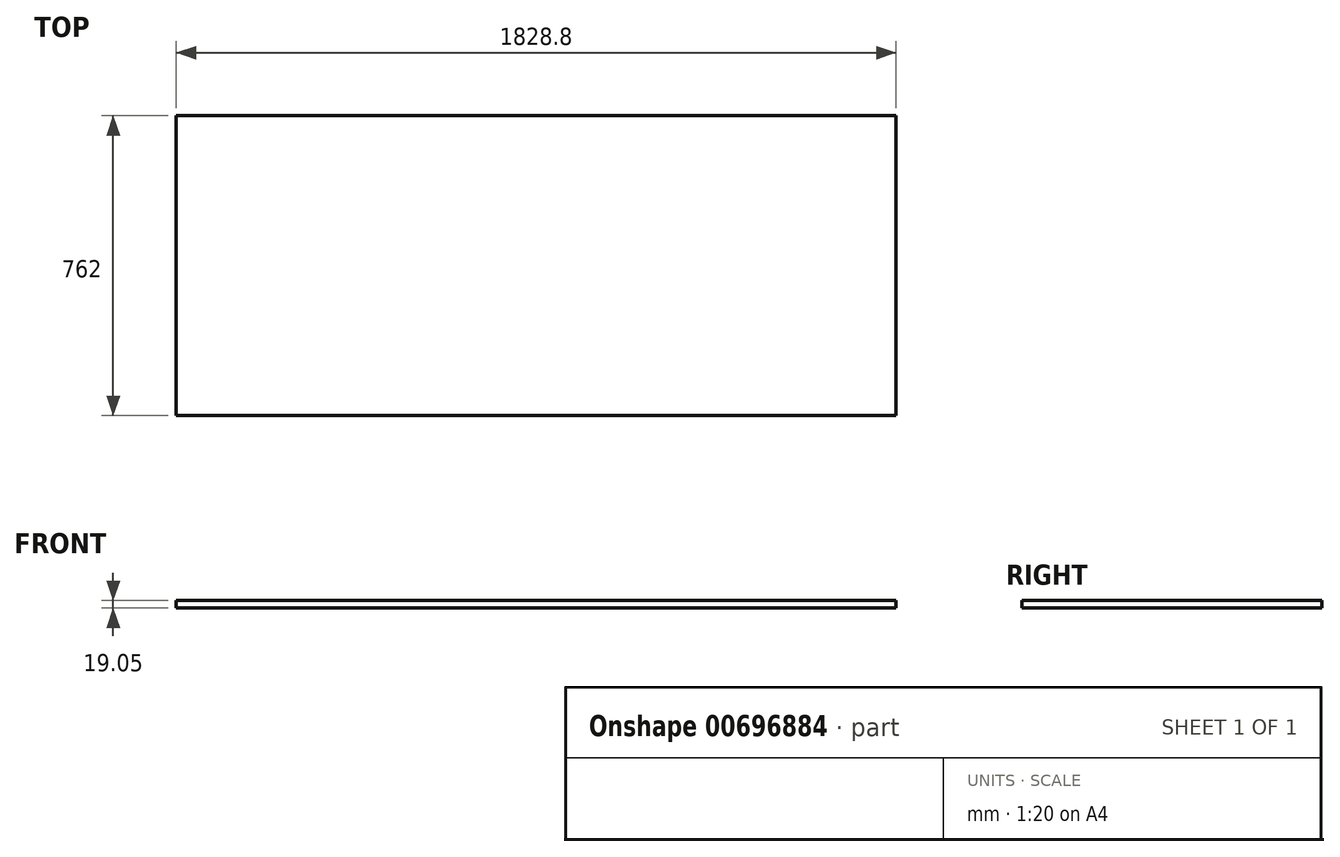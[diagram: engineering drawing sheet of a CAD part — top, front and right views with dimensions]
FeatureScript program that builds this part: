
annotation { "Feature Type Name" : "Feature", "Feature Type Description" : "" }
export const myFeature = defineFeature(function(context is Context, id is Id, definition is map)
    precondition{}
    {
        {
            var Q0;
            Q0=qCreatedBy(makeId("Top.planeOp"),FACE);
            var sketch = newSketch(context, id + "F0", { "sketchPlane" : qUnion([Q0])});
            skLineSegment(sketch, "E0.bottom", {"start": v(914.4, -381) * mm, "end": v(-914.4, -381) * mm});
            skLineSegment(sketch, "E0.top", {"start": v(914.4, 381) * mm, "end": v(-914.4, 381) * mm});
            skLineSegment(sketch, "E0.left", {"start": v(914.4, -381) * mm, "end": v(914.4, 381) * mm});
            skLineSegment(sketch, "E0.right", {"start": v(-914.4, -381) * mm, "end": v(-914.4, 381) * mm});
            skPoint(sketch, "E0.middle", {"position": v(0, 0) * mm});
            skSolve(sketch);
        }
        {
            var Q0;
            Q0=makeQuery(id+"F0.imprint","IMPRINT",FACE,{"disambiguationData":[TD([[makeQuery(id+"F0.imprint","IMPRINT",EDGE,{"derivedFrom":sQuery(id+"F0.wireOp",EDGE,"E0.bottom")}),-1.0]])]});
            extrude(context, id + "F1", {"entities" : qUnion([Q0]), "depth" : 19.05 * mm, "offsetDistance" : 25.4 * mm});
        }
    });
